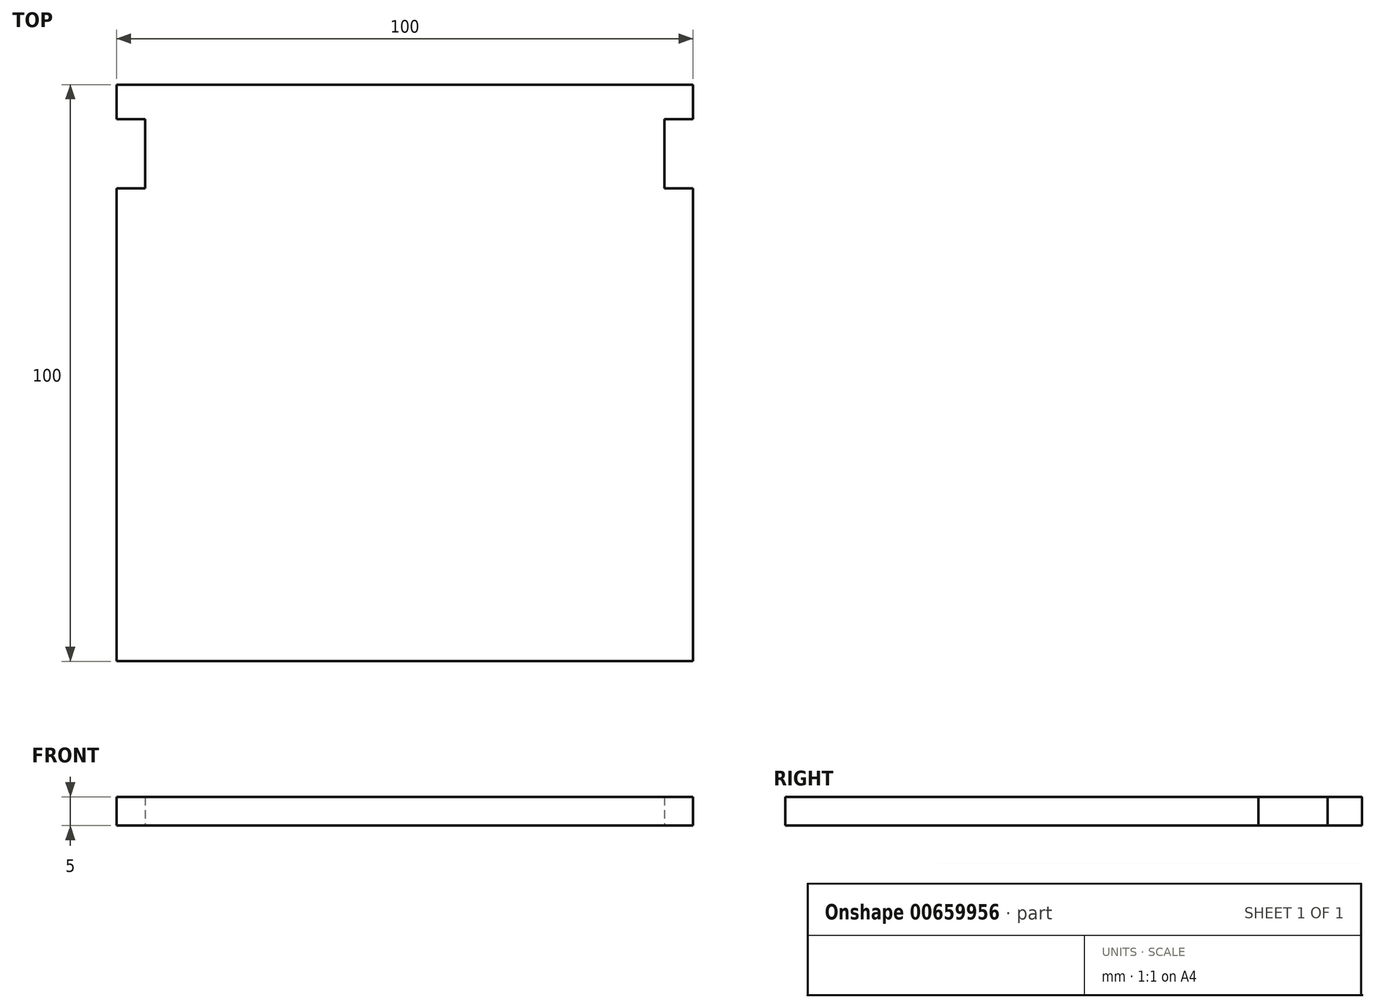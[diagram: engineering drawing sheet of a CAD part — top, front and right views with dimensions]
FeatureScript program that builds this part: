
annotation { "Feature Type Name" : "Feature", "Feature Type Description" : "" }
export const myFeature = defineFeature(function(context is Context, id is Id, definition is map)
    precondition{}
    {
        {
            var Q0;
            Q0=qCreatedBy(makeId("Top.planeOp"),FACE);
            var sketch = newSketch(context, id + "F0", { "sketchPlane" : qUnion([Q0])});
            skLineSegment(sketch, "E0.bottom", {"start": v(0, 84.97) * mm, "end": v(100, 84.97) * mm});
            skLineSegment(sketch, "E0.top", {"start": v(0, -15.03) * mm, "end": v(100, -15.03) * mm});
            skLineSegment(sketch, "E0.left", {"start": v(0, 84.97) * mm, "end": v(0, -15.03) * mm});
            skLineSegment(sketch, "E0.right", {"start": v(100, 84.97) * mm, "end": v(100, -15.03) * mm});
            skLineSegment(sketch, "E1.left", {"start": v(0, 84.97) * mm, "end": v(0, 79.97) * mm});
            skLineSegment(sketch, "E2.left", {"start": v(100, 84.97) * mm, "end": v(100, 79.97) * mm});
            skLineSegment(sketch, "E3.bottom", {"start": v(0, 78.97) * mm, "end": v(5, 78.97) * mm});
            skLineSegment(sketch, "E3.top", {"start": v(0, 66.97) * mm, "end": v(5, 66.97) * mm});
            skLineSegment(sketch, "E3.left", {"start": v(0, 78.97) * mm, "end": v(0, 66.97) * mm});
            skLineSegment(sketch, "E3.right", {"start": v(5, 78.97) * mm, "end": v(5, 66.97) * mm});
            skLineSegment(sketch, "E4.bottom", {"start": v(100, 78.97) * mm, "end": v(95, 78.97) * mm});
            skLineSegment(sketch, "E4.top", {"start": v(100, 66.97) * mm, "end": v(95, 66.97) * mm});
            skLineSegment(sketch, "E4.left", {"start": v(100, 78.97) * mm, "end": v(100, 66.97) * mm});
            skLineSegment(sketch, "E4.right", {"start": v(95, 78.97) * mm, "end": v(95, 66.97) * mm});
            skSolve(sketch);
        }
        {
            var Q0;
            Q0=makeQuery(id+"F0.imprint","IMPRINT",FACE,{"disambiguationData":[TD([[makeQuery(id+"F0.imprint","IMPRINT",EDGE,{"derivedFrom":sQuery(id+"F0.wireOp",EDGE,"E0.bottom")}),-1.0]])]});
            extrude(context, id + "F1", {"entities" : qUnion([Q0]), "depth" : 5 * mm, "offsetDistance" : 25 * mm});
        }
    });
